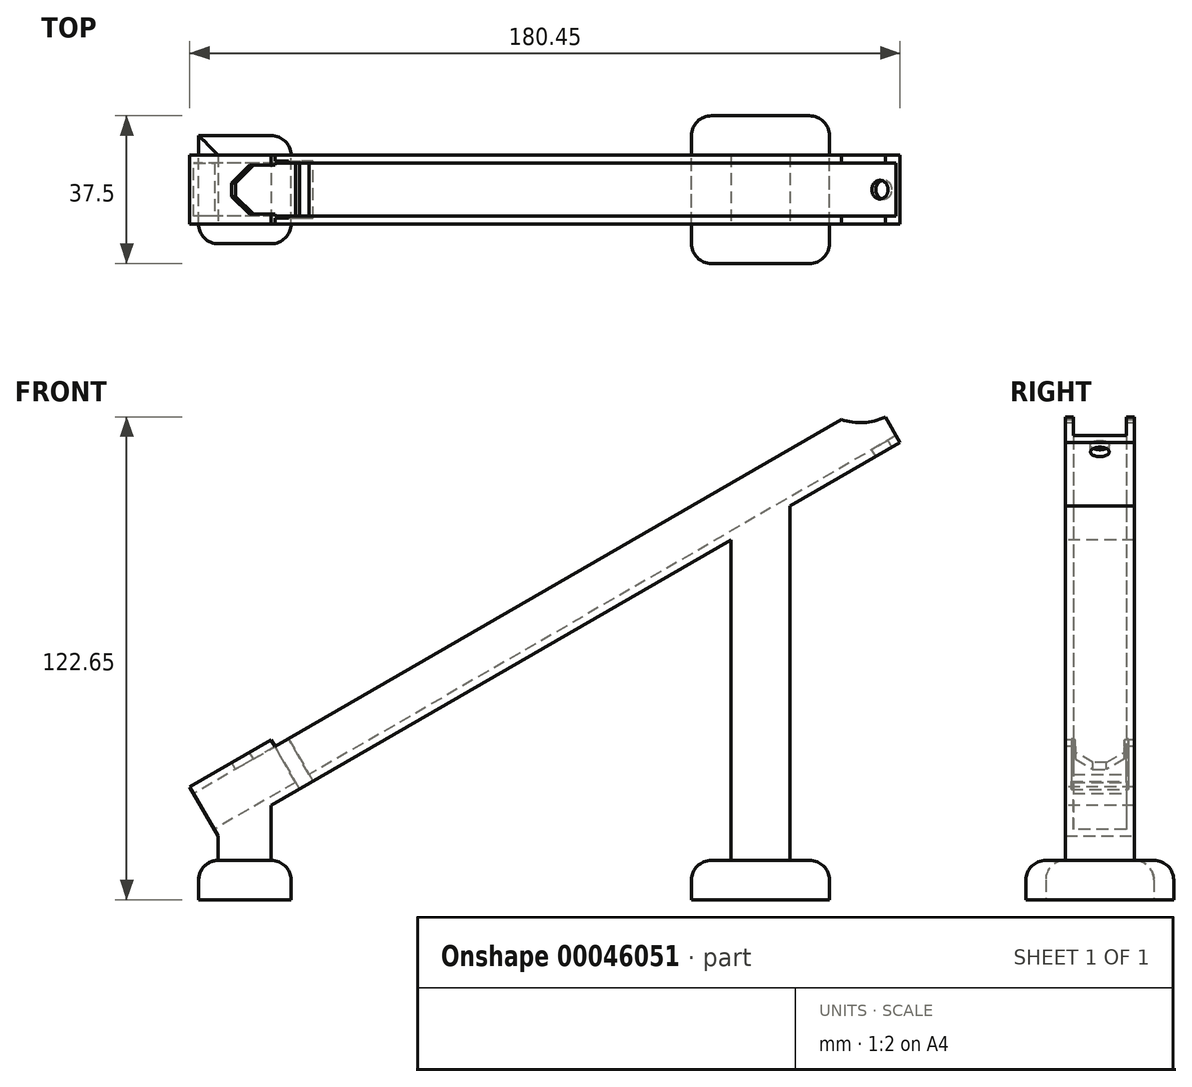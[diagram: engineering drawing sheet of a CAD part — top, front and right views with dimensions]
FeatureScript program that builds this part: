
annotation { "Feature Type Name" : "Feature", "Feature Type Description" : "" }
export const myFeature = defineFeature(function(context is Context, id is Id, definition is map)
    precondition{}
    {
        {
            var Q0;
            Q0=qCreatedBy(makeId("Top.planeOp"),FACE);
            var sketch = newSketch(context, id + "F0", { "sketchPlane" : qUnion([Q0])});
            skLineSegment(sketch, "E0", {"start": v(-122.26, 18.95) * mm, "end": v(77.74, 18.95) * mm});
            skLineSegment(sketch, "E1", {"start": v(77.74, 18.95) * mm, "end": v(77.74, 1.45) * mm});
            skLineSegment(sketch, "E2", {"start": v(77.74, 1.45) * mm, "end": v(-122.26, 1.45) * mm});
            skLineSegment(sketch, "E3", {"start": v(-122.26, 1.45) * mm, "end": v(-122.26, 18.95) * mm});
            skSolve(sketch);
        }
        {
            var Q0;
            Q0=qSketchRegion(id+"F0",true);
            extrude(context, id + "F1", {"entities" : qUnion([Q0]), "depth" : 12.5 * mm});
        }
        {
            var Q0;
            Q0=makeQuery(id+"F1.opExtrude","SWEPT_FACE",FACE,{"disambiguationData":[OSD([sQuery(id+"F0.wireOp",EDGE,"E2")])]});
            var sketch = newSketch(context, id + "F2", { "sketchPlane" : qUnion([Q0])});
            skLineSegment(sketch, "E4", {"start": v(-122.26, 0) * mm, "end": v(27.74, -86.6) * mm, "construction": true});
            skLineSegment(sketch, "E5", {"start": v(77.74, 0) * mm, "end": v(27.74, -86.6) * mm});
            skSolve(sketch);
        }
        {
            var Q0;
            Q0=makeQuery(id+"F1.opExtrude","SWEPT_FACE",FACE,{"disambiguationData":[OSD([sQuery(id+"F0.wireOp",EDGE,"E3")])]});
            var sketch = newSketch(context, id + "F3", { "sketchPlane" : qUnion([Q0])});
            skLineSegment(sketch, "E6", {"start": v(-16.95, 12.5) * mm, "end": v(-16.95, 2) * mm});
            skLineSegment(sketch, "E7", {"start": v(-16.95, 2) * mm, "end": v(-3.45, 2) * mm});
            skLineSegment(sketch, "E8", {"start": v(-3.45, 2) * mm, "end": v(-3.45, 12.5) * mm});
            skLineSegment(sketch, "E9", {"start": v(-3.45, 12.5) * mm, "end": v(-16.95, 12.5) * mm});
            skSolve(sketch);
        }
        {
            var Q0;
            Q0=qSketchRegion(id+"F3",true);
            extrude(context, id + "F4", {"entities" : qUnion([Q0]), "operationType" : NewBodyOperationType.REMOVE, "endBound" : BoundingType.THROUGH_ALL, "oppositeDirection" : true, "depth" : 25.4 * mm});
        }
        {
            var Q0;
            Q0=makeQuery(id+"F1.opExtrude","SWEPT_FACE",FACE,{"disambiguationData":[OSD([sQuery(id+"F0.wireOp",EDGE,"E0")])]});
            var sketch = newSketch(context, id + "F5", { "sketchPlane" : qUnion([Q0])});
            skLineSegment(sketch, "E10", {"start": v(-77.74, 12.5) * mm, "end": v(-77.74, 7.5) * mm});
            skLineSegment(sketch, "E11", {"start": v(-77.74, 12.5) * mm, "end": v(-67.74, 12.5) * mm});
            skArc(sketch, "E12", {"start": v(-77.74, 7.5) * mm, "mid": v(-72.25, 9.03) * mm, "end": v(-67.74, 12.5) * mm});
            skSolve(sketch);
        }
        {
            var Q0;
            Q0=qSketchRegion(id+"F5",true);
            extrude(context, id + "F6", {"entities" : qUnion([Q0]), "operationType" : NewBodyOperationType.REMOVE, "endBound" : BoundingType.THROUGH_ALL, "oppositeDirection" : true, "depth" : 25.4 * mm});
        }
        {
            var Q0;
            Q0=makeQuery(id+"F4.boolean.opBoolean","COPY",FACE,{"derivedFrom":makeQuery(id+"F4.opExtrude","SWEPT_FACE",FACE,{"disambiguationData":[OSD([sQuery(id+"F3.wireOp",EDGE,"E7")])]})});
            var sketch = newSketch(context, id + "F7", { "sketchPlane" : qUnion([Q0])});
            skLineSegment(sketch, "E13", {"start": v(77.74, 10.2) * mm, "end": v(72.98, 10.2) * mm});
            skLineSegment(sketch, "E14", {"start": v(72.98, 10.2) * mm, "end": v(72.98, 16.95) * mm});
            skLineSegment(sketch, "E15", {"start": v(72.98, 10.2) * mm, "end": v(72.98, 3.45) * mm});
            skCircle(sketch, "E16", {"center": v(72.98, 10.2) * mm, "radius": 2.38 * mm});
            skSolve(sketch);
        }
        {
            var Q0;
            Q0=qSketchRegion(id+"F7",true);
            extrude(context, id + "F8", {"entities" : qUnion([Q0]), "operationType" : NewBodyOperationType.REMOVE, "endBound" : BoundingType.THROUGH_ALL, "oppositeDirection" : true, "depth" : 25.4 * mm});
        }
        {
            var Q0;
            Q0=makeQuery(id+"F1.opExtrude","CAP_FACE",FACE,{"disambiguationData":[OSD([sQuery(id+"F0.wireOp",EDGE,"E0"),sQuery(id+"F0.wireOp",EDGE,"E1"),sQuery(id+"F0.wireOp",EDGE,"E2"),sQuery(id+"F0.wireOp",EDGE,"E3")])],"isStart":true});
            var sketch = newSketch(context, id + "F9", { "sketchPlane" : qUnion([Q0])});
            skLineSegment(sketch, "E17", {"start": v(-122.26, -1.45) * mm, "end": v(-98.45, -1.45) * mm});
            skLineSegment(sketch, "E18", {"start": v(-122.26, -18.95) * mm, "end": v(-98.45, -18.95) * mm});
            skLineSegment(sketch, "E19", {"start": v(-98.45, -1.45) * mm, "end": v(-98.45, -18.95) * mm});
            skLineSegment(sketch, "E20", {"start": v(-98.45, -2.95) * mm, "end": v(-94.45, -2.95) * mm});
            skLineSegment(sketch, "E21", {"start": v(-94.45, -2.95) * mm, "end": v(-94.45, -17.45) * mm});
            skLineSegment(sketch, "E22", {"start": v(-94.45, -17.45) * mm, "end": v(-98.45, -17.45) * mm});
            skSolve(sketch);
        }
        {
            var Q0;
            {var subQ1=sQuery(id+"F9.wireOp",EDGE,"E20");Q0=makeQuery(id+"F9.imprint","IMPRINT",FACE,{"disambiguationData":[TD([[makeQuery(id+"F9.imprint","IMPRINT",EDGE,{"derivedFrom":subQ1}),-1.0]])]});}
            extrude(context, id + "F10", {"entities" : qUnion([Q0]), "operationType" : NewBodyOperationType.REMOVE, "endBound" : BoundingType.THROUGH_ALL, "oppositeDirection" : true, "depth" : 25.4 * mm});
        }
        {
            var Q0;
            Q0=makeQuery(id+"F1.opExtrude","SWEPT_FACE",FACE,{"disambiguationData":[OSD([sQuery(id+"F0.wireOp",EDGE,"E3")])]});
            var sketch = newSketch(context, id + "F11", { "sketchPlane" : qUnion([Q0])});
            skLineSegment(sketch, "E23", {"start": v(-18.95, 12.5) * mm, "end": v(-18.95, 14.5) * mm});
            skLineSegment(sketch, "E24", {"start": v(-18.95, 14.5) * mm, "end": v(-1.45, 14.5) * mm});
            skLineSegment(sketch, "E25", {"start": v(-1.45, 14.5) * mm, "end": v(-1.45, 12.5) * mm});
            skLineSegment(sketch, "E26", {"start": v(-1.45, 12.5) * mm, "end": v(-18.95, 12.5) * mm});
            skSolve(sketch);
        }
        {
            var Q0;
            {var subQ4=sQuery(id+"F11.wireOp",EDGE,"E23");Q0=makeQuery(id+"F11.imprint","IMPRINT",FACE,{"disambiguationData":[TD([[makeQuery(id+"F11.imprint","IMPRINT",EDGE,{"derivedFrom":subQ4}),-1.0]])]});}
            extrude(context, id + "F12", {"entities" : qUnion([Q0]), "operationType" : NewBodyOperationType.ADD, "oppositeDirection" : true, "depth" : 23.8 * mm});
        }
        {
            var Q0;
            Q0=makeQuery(id+"F12.opExtrude","SWEPT_FACE",FACE,{"disambiguationData":[OSD([sQuery(id+"F11.wireOp",EDGE,"E24")])]});
            var sketch = newSketch(context, id + "F13", { "sketchPlane" : qUnion([Q0])});
            skLineSegment(sketch, "E27.left", {"start": v(-98.45, 16.45) * mm, "end": v(-98.45, 3.95) * mm});
            skLineSegment(sketch, "E28", {"start": v(-109.95, 11.92) * mm, "end": v(-109.95, 8.48) * mm});
            skLineSegment(sketch, "E29", {"start": v(-109.95, 11.92) * mm, "end": v(-104.77, 16.45) * mm});
            skLineSegment(sketch, "E30", {"start": v(-109.95, 8.48) * mm, "end": v(-104.77, 3.95) * mm});
            skLineSegment(sketch, "E31", {"start": v(-104.77, 3.95) * mm, "end": v(-98.45, 3.95) * mm});
            skLineSegment(sketch, "E32", {"start": v(-98.45, 16.45) * mm, "end": v(-104.77, 16.45) * mm});
            skPoint(sketch, "E33", {"position": v(-98.45, 10.2) * mm});
            skSolve(sketch);
        }
        {
            var Q0;
            Q0=qSketchRegion(id+"F13",true);
            var Q1;
            Q1=makeQuery(id+"F12.opExtrude","SWEPT_FACE",FACE,{"disambiguationData":[OSD([sQuery(id+"F11.wireOp",EDGE,"E26")])]});
            extrude(context, id + "F14", {"entities" : qUnion([Q0]), "operationType" : NewBodyOperationType.REMOVE, "endBound" : BoundingType.UP_TO_SURFACE, "oppositeDirection" : true, "endBoundEntityFace" : qUnion([Q1]), "depth" : 2 * mm});
        }
        {
            var Q0;
            {var subQ0=sQuery(id+"F0.wireOp",EDGE,"E2");Q0=makeQuery(id+"F2.imprint","IMPRINT",FACE,{"disambiguationData":[TD([[makeQuery(id+"F2.imprint","IMPRINT",EDGE,{"derivedFrom":makeQuery(id+"F1.opExtrude","CAP_EDGE",EDGE,{"disambiguationData":[OSD([subQ0])],"isStart":true})}),-1.0]])]});}
            var sketch = newSketch(context, id + "F15", { "sketchPlane" : qUnion([Q0])});
            skLineSegment(sketch, "E34", {"start": v(45.44, 0) * mm, "end": v(-4.56, -86.6) * mm});
            skLineSegment(sketch, "E35", {"start": v(28.12, 0) * mm, "end": v(-17.55, -79.1) * mm});
            skLineSegment(sketch, "E36", {"start": v(-17.55, -79.1) * mm, "end": v(-4.56, -86.6) * mm});
            skLineSegment(sketch, "E37", {"start": v(-17.55, -79.1) * mm, "end": v(-130.34, -13.99) * mm, "construction": true});
            skLineSegment(sketch, "E38", {"start": v(-106.72, 0) * mm, "end": v(-118.68, -20.71) * mm});
            skLineSegment(sketch, "E39", {"start": v(-118.68, -20.71) * mm, "end": v(-130.34, -13.99) * mm});
            skLineSegment(sketch, "E40", {"start": v(-130.34, -13.99) * mm, "end": v(-122.26, 0) * mm});
            skSolve(sketch);
        }
        {
            var Q0;
            {var subQ2=sQuery(id+"F15.wireOp",EDGE,"E38");Q0=makeQuery(id+"F15.imprint","IMPRINT",FACE,{"disambiguationData":[TD([[makeQuery(id+"F15.imprint","IMPRINT",EDGE,{"derivedFrom":subQ2}),-1.0]])]});}
            var Q1;
            {var subQ2=sQuery(id+"F15.wireOp",EDGE,"E34");Q1=makeQuery(id+"F15.imprint","IMPRINT",FACE,{"disambiguationData":[TD([[makeQuery(id+"F15.imprint","IMPRINT",EDGE,{"derivedFrom":subQ2}),-1.0]])]});}
            var Q2;
            Q2=makeQuery(id+"F12.boolean.opBoolean","MERGE",FACE,{"derivedFrom":[makeQuery(id+"F1.opExtrude","SWEPT_FACE",FACE,{"disambiguationData":[OSD([sQuery(id+"F0.wireOp",EDGE,"E0")])]}),makeQuery(id+"F12.opExtrude","SWEPT_FACE",FACE,{"disambiguationData":[OSD([sQuery(id+"F11.wireOp",EDGE,"E23")])]})]});
            extrude(context, id + "F16", {"entities" : qUnion([Q0, Q1]), "operationType" : NewBodyOperationType.ADD, "endBound" : BoundingType.UP_TO_SURFACE, "oppositeDirection" : true, "endBoundEntityFace" : qUnion([Q2]), "depth" : 25 * mm});
        }
        {
            var Q0;
            Q0=makeQuery(id+"F1.opExtrude","SWEPT_BODY",BODY,{"disambiguationData":[OSD([sQuery(id+"F0.wireOp",EDGE,"E0"),sQuery(id+"F0.wireOp",EDGE,"E1"),sQuery(id+"F0.wireOp",EDGE,"E2"),sQuery(id+"F0.wireOp",EDGE,"E3")])]});
            var Q1;
            Q1=sQuery(id+"F0.wireOp",EDGE,"E3");
            transform(context, id + "F17", {"entities" : qUnion([Q0]), "transformType" : TransformType.ROTATION, "transformAxis" : qUnion([Q1]), "angle" : 330 * degree, "makeCopy" : false});
        }
        {
            var Q0;
            Q0=makeQuery(id+"F16.opExtrude","SWEPT_FACE",FACE,{"disambiguationData":[OSD([sQuery(id+"F15.wireOp",EDGE,"E39")])]});
            var sketch = newSketch(context, id + "F18", { "sketchPlane" : qUnion([Q0])});
            skLineSegment(sketch, "E41", {"start": v(-122.26, -10.2) * mm, "end": v(-108.8, -10.2) * mm, "construction": true});
            skLineSegment(sketch, "E42", {"start": v(-115.53, -18.95) * mm, "end": v(-115.53, -1.45) * mm, "construction": true});
            skLineSegment(sketch, "E43.bottom", {"start": v(-127.26, 3.55) * mm, "end": v(-103.8, 3.55) * mm});
            skLineSegment(sketch, "E43.top", {"start": v(-127.26, -23.95) * mm, "end": v(-103.8, -23.95) * mm});
            skLineSegment(sketch, "E43.left", {"start": v(-127.26, 3.55) * mm, "end": v(-127.26, -23.95) * mm});
            skLineSegment(sketch, "E43.right", {"start": v(-103.8, 3.55) * mm, "end": v(-103.8, -23.95) * mm});
            skLineSegment(sketch, "E44", {"start": v(15.47, -18.95) * mm, "end": v(15.47, -1.45) * mm, "construction": true});
            skLineSegment(sketch, "E45", {"start": v(7.97, -10.2) * mm, "end": v(22.97, -10.2) * mm, "construction": true});
            skLineSegment(sketch, "E46.bottom", {"start": v(-2.03, 8.55) * mm, "end": v(32.97, 8.55) * mm});
            skLineSegment(sketch, "E46.top", {"start": v(-2.03, -28.95) * mm, "end": v(32.97, -28.95) * mm});
            skLineSegment(sketch, "E46.left", {"start": v(-2.03, 8.55) * mm, "end": v(-2.03, -28.95) * mm});
            skLineSegment(sketch, "E46.right", {"start": v(32.97, 8.55) * mm, "end": v(32.97, -28.95) * mm});
            skSolve(sketch);
        }
        {
            var Q0;
            Q0=makeQuery(id+"F18.imprint","IMPRINT",FACE,{"disambiguationData":[TD([[makeQuery(id+"F18.imprint","IMPRINT",EDGE,{"derivedFrom":sQuery(id+"F18.wireOp",EDGE,"E46.bottom")}),-1.0]])]});
            var Q1;
            Q1=makeQuery(id+"F18.imprint","IMPRINT",FACE,{"disambiguationData":[TD([[makeQuery(id+"F18.imprint","IMPRINT",EDGE,{"derivedFrom":sQuery(id+"F18.wireOp",EDGE,"E43.bottom")}),-1.0]])]});
            extrude(context, id + "F19", {"entities" : qUnion([Q0, Q1]), "operationType" : NewBodyOperationType.ADD, "oppositeDirection" : true, "depth" : 10 * mm});
        }
        {
            var Q0;
            Q0=makeQuery(id+"F19.opExtrude","CAP_EDGE",EDGE,{"disambiguationData":[OSD([sQuery(id+"F18.wireOp",EDGE,"E43.left")])],"isStart":false});
            var Q1;
            Q1=makeQuery(id+"F19.opExtrude","CAP_EDGE",EDGE,{"disambiguationData":[OSD([sQuery(id+"F18.wireOp",EDGE,"E43.bottom")])],"isStart":false});
            var Q2;
            Q2=makeQuery(id+"F19.opExtrude","CAP_EDGE",EDGE,{"disambiguationData":[OSD([sQuery(id+"F18.wireOp",EDGE,"E43.right")])],"isStart":false});
            var Q3;
            Q3=makeQuery(id+"F19.opExtrude","CAP_EDGE",EDGE,{"disambiguationData":[OSD([sQuery(id+"F18.wireOp",EDGE,"E43.top")])],"isStart":false});
            var Q4;
            Q4=makeQuery(id+"F19.opExtrude","CAP_EDGE",EDGE,{"disambiguationData":[OSD([sQuery(id+"F18.wireOp",EDGE,"E46.left")])],"isStart":false});
            var Q5;
            Q5=makeQuery(id+"F19.opExtrude","CAP_EDGE",EDGE,{"disambiguationData":[OSD([sQuery(id+"F18.wireOp",EDGE,"E46.top")])],"isStart":false});
            var Q6;
            Q6=makeQuery(id+"F19.opExtrude","CAP_EDGE",EDGE,{"disambiguationData":[OSD([sQuery(id+"F18.wireOp",EDGE,"E46.bottom")])],"isStart":false});
            var Q7;
            Q7=makeQuery(id+"F19.opExtrude","CAP_EDGE",EDGE,{"disambiguationData":[OSD([sQuery(id+"F18.wireOp",EDGE,"E46.right")])],"isStart":false});
            fillet(context, id + "F20", {"entities" : qUnion([Q0, Q1, Q2, Q3, Q4, Q5, Q6, Q7]), "radius" : 5 * mm, "tangentPropagation" : true, "allowEdgeOverflow" : false});
        }
        {
            var Q0;
            Q0=makeQuery(id+"F20.opFillet","BLEND_EDGE",EDGE,{"blendedFrom":[makeQuery(id+"F19.opExtrude","CAP_EDGE",EDGE,{"disambiguationData":[OSD([sQuery(id+"F18.wireOp",EDGE,"E43.bottom")])],"isStart":false}),makeQuery(id+"F19.opExtrude","CAP_EDGE",EDGE,{"disambiguationData":[OSD([sQuery(id+"F18.wireOp",EDGE,"E43.left")])],"isStart":false})],"blendedInto":[]});
            var Q1;
            Q1=makeQuery(id+"F20.opFillet","BLEND_EDGE",EDGE,{"blendedFrom":[makeQuery(id+"F19.opExtrude","CAP_EDGE",EDGE,{"disambiguationData":[OSD([sQuery(id+"F18.wireOp",EDGE,"E43.bottom")])],"isStart":false}),makeQuery(id+"F19.opExtrude","CAP_EDGE",EDGE,{"disambiguationData":[OSD([sQuery(id+"F18.wireOp",EDGE,"E43.right")])],"isStart":false})],"blendedInto":[]});
            var Q2;
            Q2=makeQuery(id+"F20.opFillet","BLEND_EDGE",EDGE,{"blendedFrom":[makeQuery(id+"F19.opExtrude","CAP_EDGE",EDGE,{"disambiguationData":[OSD([sQuery(id+"F18.wireOp",EDGE,"E43.top")])],"isStart":false}),makeQuery(id+"F19.opExtrude","CAP_EDGE",EDGE,{"disambiguationData":[OSD([sQuery(id+"F18.wireOp",EDGE,"E43.right")])],"isStart":false})],"blendedInto":[]});
            var Q3;
            Q3=makeQuery(id+"F20.opFillet","BLEND_EDGE",EDGE,{"blendedFrom":[makeQuery(id+"F19.opExtrude","CAP_EDGE",EDGE,{"disambiguationData":[OSD([sQuery(id+"F18.wireOp",EDGE,"E46.bottom")])],"isStart":false}),makeQuery(id+"F19.opExtrude","CAP_EDGE",EDGE,{"disambiguationData":[OSD([sQuery(id+"F18.wireOp",EDGE,"E46.right")])],"isStart":false})],"blendedInto":[]});
            var Q4;
            Q4=makeQuery(id+"F20.opFillet","BLEND_EDGE",EDGE,{"blendedFrom":[makeQuery(id+"F19.opExtrude","CAP_EDGE",EDGE,{"disambiguationData":[OSD([sQuery(id+"F18.wireOp",EDGE,"E46.top")])],"isStart":false}),makeQuery(id+"F19.opExtrude","CAP_EDGE",EDGE,{"disambiguationData":[OSD([sQuery(id+"F18.wireOp",EDGE,"E46.right")])],"isStart":false})],"blendedInto":[]});
            var Q5;
            Q5=makeQuery(id+"F20.opFillet","BLEND_EDGE",EDGE,{"blendedFrom":[makeQuery(id+"F19.opExtrude","CAP_EDGE",EDGE,{"disambiguationData":[OSD([sQuery(id+"F18.wireOp",EDGE,"E46.top")])],"isStart":false}),makeQuery(id+"F19.opExtrude","CAP_EDGE",EDGE,{"disambiguationData":[OSD([sQuery(id+"F18.wireOp",EDGE,"E46.left")])],"isStart":false})],"blendedInto":[]});
            var Q6;
            Q6=makeQuery(id+"F20.opFillet","BLEND_EDGE",EDGE,{"blendedFrom":[makeQuery(id+"F19.opExtrude","CAP_EDGE",EDGE,{"disambiguationData":[OSD([sQuery(id+"F18.wireOp",EDGE,"E46.bottom")])],"isStart":false}),makeQuery(id+"F19.opExtrude","CAP_EDGE",EDGE,{"disambiguationData":[OSD([sQuery(id+"F18.wireOp",EDGE,"E46.left")])],"isStart":false})],"blendedInto":[]});
            fillet(context, id + "F21", {"entities" : qUnion([Q0, Q1, Q2, Q3, Q4, Q5, Q6]), "radius" : 5 * mm, "tangentPropagation" : true, "allowEdgeOverflow" : false});
        }
    });
